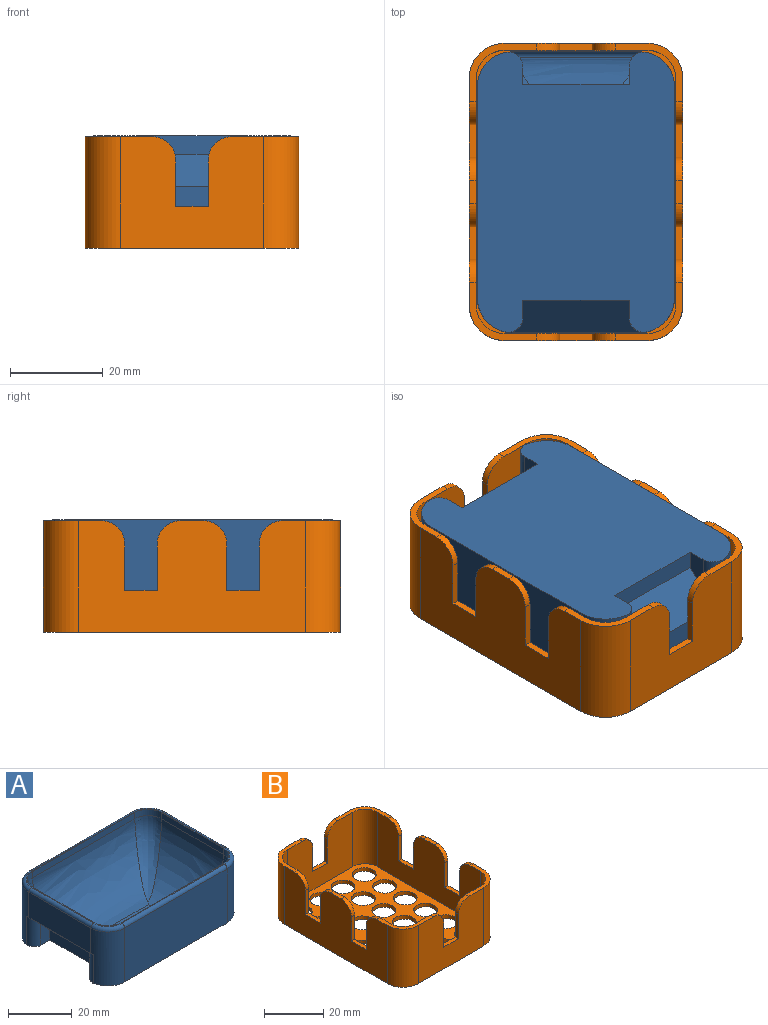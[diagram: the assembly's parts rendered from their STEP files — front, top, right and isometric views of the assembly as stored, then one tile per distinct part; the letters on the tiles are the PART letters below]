
ASSEMBLY  parts=2 mates=1
PART A: 47 faces, bbox 63.4x45.4x23.6 mm
  f0: plane 60.37x42.5mm, normal (0,0,-1), area 2192.5mm2, adj f3,f5,f6,f7,f8,f9,f28,f29
  f1: plane 58x40mm, normal (0,0,1), area 64.5mm2, adj f10,f11,f12,f13,f15,f16,f17,f18
  f2: plane 27.5x9.75mm, normal (-1,0,0), area 268.1mm2, adj f6,f9,f32,f46
  f3: plane 45.5x20.75mm, normal (0,-1,0), area 944.1mm2, adj f0,f6,f7,f42
  f4: plane 27.5x9.75mm, normal (1,0,0), area 268.1mm2, adj f7,f8,f27,f39
  f5: plane 45.5x20.75mm, normal (0,1,0), area 944.1mm2, adj f0,f8,f9,f43
  f6: cylinder r=7.5mm len=20.75mm, axis (0,0,1), area 230.7mm2, adj f0,f2,f3,f32,f38,f44
  f7: cylinder r=7.5mm len=20.75mm, axis (0,0,-1), area 230.7mm2, adj f0,f3,f4,f27,f36,f40
  f8: cylinder r=7.5mm len=20.75mm, axis (0,0,1), area 230.7mm2, adj f0,f4,f5,f27,f35,f41
  f9: cylinder r=7.5mm len=20.75mm, axis (0,0,-1), area 230.7mm2, adj f0,f2,f5,f32,f37,f45
  f10: plane 27.5x2.4mm, normal (1,0,0), area 66mm2, adj f1,f15,f18,f26
  f11: plane 45.5x2.4mm, normal (0,1,0), area 109.2mm2, adj f1,f15,f16,f22
  f12: plane 27.5x2.4mm, normal (-1,0,0), area 66mm2, adj f1,f16,f17,f19
  f13: plane 45.5x2.4mm, normal (0,-1,0), area 109.2mm2, adj f1,f17,f18,f23
  f14: plane 21.3x3.3mm, normal (0,0,1), area 70.3mm2, adj f19,f22,f23,f26
  f15: cylinder r=5.9mm len=5.9mm, axis (0,0,1), area 22.2mm2, adj f1,f10,f11,f24
  f16: cylinder r=5.9mm len=5.9mm, axis (0,0,-1), area 22.2mm2, adj f1,f11,f12,f20
  f17: cylinder r=5.9mm len=5.9mm, axis (0,0,1), area 22.2mm2, adj f1,f12,f13,f21
  f18: cylinder r=5.9mm len=5.9mm, axis (0,0,-1), area 22.2mm2, adj f1,f10,f13,f25
  f19: bspline ~27.5x18mm, area 524mm2, adj f12,f14,f20,f21
  f20: bspline ~19.65x18mm, area 121.3mm2, adj f16,f19,f22
  f21: bspline ~19.65x18mm, area 121.3mm2, adj f17,f19,f23
  f22: bspline ~45.5x18mm, area 941.5mm2, adj f11,f14,f20,f24
  f23: bspline ~45.5x18mm, area 941.5mm2, adj f13,f14,f21,f25
  f24: bspline ~19.65x18mm, area 121.3mm2, adj f15,f22,f26
  f25: bspline ~19.65x18mm, area 121.3mm2, adj f18,f23,f26
  f26: bspline ~27.5x18mm, area 521.8mm2, adj f10,f14,f24,f25
  f27: plane 31.65x8.65mm, normal (0.71,0,-0.71), area 233.7mm2, adj f4,f7,f8,f28,f29,f30,f35,f36
  f28: plane 23x4mm, normal (1,0,0), area 92mm2, adj f0,f27,f29,f30
  f29: plane 7.94x3.94mm, normal (0,1,0), area 23.5mm2, adj f0,f27,f28,f36
  f30: plane 7.94x3.94mm, normal (0,-1,0), area 23.5mm2, adj f0,f27,f28,f35
  f31: plane 23x4mm, normal (-1,0,0), area 92mm2, adj f0,f32,f33,f34
  f32: plane 31.65x8.65mm, normal (-0.71,0,-0.71), area 233.7mm2, adj f2,f6,f9,f31,f33,f34,f37,f38
  f33: plane 7.94x3.94mm, normal (0,1,0), area 23.5mm2, adj f0,f31,f32,f38
  f34: plane 7.94x3.94mm, normal (0,-1,0), area 23.5mm2, adj f0,f31,f32,f37
  f35: cylinder r=3mm len=10.9mm, axis (0,0,1), area 49.1mm2, adj f0,f8,f27,f30
  f36: cylinder r=3mm len=10.9mm, axis (0,0,-1), area 49.1mm2, adj f0,f7,f27,f29
  f37: cylinder r=3mm len=10.9mm, axis (0,0,-1), area 49.1mm2, adj f0,f9,f32,f34
  f38: cylinder r=3mm len=10.9mm, axis (0,0,1), area 49.1mm2, adj f0,f6,f32,f33
  f39: cylinder r=1.25mm len=27.5mm, axis (0,-1,0), area 54mm2, adj f1,f4,f40,f41
  f40: torus R=6.25mm, axis (0,0,1), area 21.7mm2, adj f1,f7,f39,f42
  f41: torus R=6.25mm, axis (0,0,1), area 21.7mm2, adj f1,f8,f39,f43
  f42: cylinder r=1.25mm len=45.5mm, axis (-1,0,0), area 89.3mm2, adj f1,f3,f40,f44
  f43: cylinder r=1.25mm len=45.5mm, axis (1,0,0), area 89.3mm2, adj f1,f5,f41,f45
  f44: torus R=6.25mm, axis (0,0,1), area 21.7mm2, adj f1,f6,f42,f46
  f45: torus R=6.25mm, axis (0,0,1), area 21.7mm2, adj f1,f9,f43,f46
  f46: cylinder r=1.25mm len=27.5mm, axis (0,1,0), area 54mm2, adj f1,f2,f44,f45
PART B: 78 faces, bbox 46x64x24 mm
  f0: plane 14.5x12.5mm, normal (0,0,1), area 33.9mm2, adj f3,f5,f9,f11,f18,f23,f66,f75
  f1: plane 14.5x12.5mm, normal (0,0,1), area 33.9mm2, adj f2,f4,f9,f11,f15,f20,f68,f76
  f2: plane 31x24mm, normal (0,-1,0), area 628.3mm2, adj f1,f13,f14,f15,f16,f63,f64,f65
  f3: plane 31x24mm, normal (0,1,0), area 628.3mm2, adj f0,f8,f14,f17,f18,f60,f61,f62
  f4: plane 31x22.5mm, normal (0,1,0), area 581.8mm2, adj f1,f13,f19,f20,f21,f63,f64,f65
  f5: plane 31x22.5mm, normal (0,-1,0), area 581.8mm2, adj f0,f8,f19,f22,f23,f60,f61,f62
  f6: plane 5x1.5mm, normal (0,0,1), area 7.5mm2, adj f9,f11,f74,f77
  f7: plane 5x1.5mm, normal (0,0,1), area 7.5mm2, adj f10,f12,f70,f72
  f8: plane 14.5x12.5mm, normal (0,0,1), area 33.9mm2, adj f3,f5,f10,f12,f17,f22,f67,f73
  f9: plane 49x24mm, normal (-1,0,0), area 944.5mm2, adj f0,f1,f6,f14,f15,f18,f30,f31
  f10: plane 49x24mm, normal (1,0,0), area 944.5mm2, adj f7,f8,f13,f14,f16,f17,f24,f25
  f11: plane 49x22.5mm, normal (1,0,0), area 871mm2, adj f0,f1,f6,f19,f20,f23,f30,f31
  f12: plane 49x22.5mm, normal (-1,0,0), area 871mm2, adj f7,f8,f13,f19,f21,f22,f24,f25
  f13: plane 14.5x12.5mm, normal (0,0,1), area 33.9mm2, adj f2,f4,f10,f12,f16,f21,f69,f71
  f14: plane 64x46mm, normal (0,0,-1), area 1689.3mm2, adj f2,f3,f9,f10,f15,f16,f17,f18
  f15: cylinder r=7.5mm len=24mm, axis (0,0,1), area 282.7mm2, adj f1,f2,f9,f14
  f16: cylinder r=7.5mm len=24mm, axis (0,0,-1), area 282.7mm2, adj f2,f10,f13,f14
  f17: cylinder r=7.5mm len=24mm, axis (0,0,1), area 282.7mm2, adj f3,f8,f10,f14
  f18: cylinder r=7.5mm len=24mm, axis (0,0,-1), area 282.7mm2, adj f0,f3,f9,f14
  f19: plane 61x43mm, normal (0,0,1), area 1385.7mm2, adj f4,f5,f11,f12,f20,f21,f22,f23
  f20: cylinder r=6mm len=22.5mm, axis (0,0,1), area 212.1mm2, adj f1,f4,f11,f19
  f21: cylinder r=6mm len=22.5mm, axis (0,0,-1), area 212.1mm2, adj f4,f12,f13,f19
  f22: cylinder r=6mm len=22.5mm, axis (0,0,1), area 212.1mm2, adj f5,f8,f12,f19
  f23: cylinder r=6mm len=22.5mm, axis (0,0,-1), area 212.1mm2, adj f0,f5,f11,f19
  f24: plane 10x1.5mm, normal (0,-1,0), area 15mm2, adj f10,f12,f25,f73
  f25: plane 7x1.5mm, normal (0,0,1), area 10.5mm2, adj f10,f12,f24,f26
  f26: plane 10x1.5mm, normal (0,1,0), area 15mm2, adj f10,f12,f25,f72
  f27: plane 7x1.5mm, normal (0,0,1), area 10.5mm2, adj f10,f12,f28,f29
  f28: plane 10x1.5mm, normal (0,1,0), area 15mm2, adj f10,f12,f27,f71
  f29: plane 10x1.5mm, normal (0,-1,0), area 15mm2, adj f10,f12,f27,f70
  f30: plane 10x1.5mm, normal (0,1,0), area 15mm2, adj f9,f11,f31,f74
  f31: plane 7x1.5mm, normal (0,0,1), area 10.5mm2, adj f9,f11,f30,f32
  f32: plane 10x1.5mm, normal (0,-1,0), area 15mm2, adj f9,f11,f31,f75
  f33: plane 10x1.5mm, normal (0,-1,0), area 15mm2, adj f9,f11,f35,f77
  f34: plane 10x1.5mm, normal (0,1,0), area 15mm2, adj f9,f11,f35,f76
  f35: plane 7x1.5mm, normal (0,0,1), area 10.5mm2, adj f9,f11,f33,f34
  f36: cylinder r=4mm len=8mm, axis (0,0,1), area 37.7mm2, adj f14,f19
  f37: cylinder r=4mm len=8mm, axis (0,0,1), area 37.7mm2, adj f14,f19
  f38: cylinder r=4mm len=8mm, axis (0,0,1), area 37.7mm2, adj f14,f19
  f39: cylinder r=4mm len=8mm, axis (0,0,1), area 37.7mm2, adj f14,f19
  f40: cylinder r=4mm len=8mm, axis (0,0,1), area 37.7mm2, adj f14,f19
  f41: cylinder r=4mm len=8mm, axis (0,0,1), area 37.7mm2, adj f14,f19
  f42: cylinder r=4mm len=8mm, axis (0,0,1), area 37.7mm2, adj f14,f19
  f43: cylinder r=4mm len=8mm, axis (0,0,1), area 37.7mm2, adj f14,f19
  f44: cylinder r=4mm len=8mm, axis (0,0,1), area 37.7mm2, adj f14,f19
  f45: cylinder r=4mm len=8mm, axis (0,0,1), area 37.7mm2, adj f14,f19
  f46: cylinder r=4mm len=8mm, axis (0,0,1), area 37.7mm2, adj f14,f19
  f47: cylinder r=4mm len=8mm, axis (0,0,1), area 37.7mm2, adj f14,f19
  f48: cylinder r=4mm len=8mm, axis (0,0,1), area 37.7mm2, adj f14,f19
  f49: cylinder r=4mm len=8mm, axis (0,0,1), area 37.7mm2, adj f14,f19
  f50: cylinder r=4mm len=8mm, axis (0,0,1), area 37.7mm2, adj f14,f19
  f51: cylinder r=4mm len=8mm, axis (0,0,1), area 37.7mm2, adj f14,f19
  f52: cylinder r=4mm len=8mm, axis (0,0,1), area 37.7mm2, adj f14,f19
  f53: cylinder r=4mm len=8mm, axis (0,0,1), area 37.7mm2, adj f14,f19
  f54: cylinder r=4mm len=8mm, axis (0,0,1), area 37.7mm2, adj f14,f19
  f55: cylinder r=4mm len=8mm, axis (0,0,1), area 37.7mm2, adj f14,f19
  f56: cylinder r=4mm len=8mm, axis (0,0,1), area 37.7mm2, adj f14,f19
  f57: cylinder r=4mm len=8mm, axis (0,0,1), area 37.7mm2, adj f14,f19
  f58: cylinder r=4mm len=8mm, axis (0,0,1), area 37.7mm2, adj f14,f19
  f59: cylinder r=4mm len=8mm, axis (0,0,1), area 37.7mm2, adj f14,f19
  f60: plane 7x1.5mm, normal (0,0,1), area 10.5mm2, adj f3,f5,f61,f62
  f61: plane 10x1.5mm, normal (-1,0,0), area 15mm2, adj f3,f5,f60,f67
  f62: plane 10x1.5mm, normal (1,0,0), area 15mm2, adj f3,f5,f60,f66
  f63: plane 10x1.5mm, normal (1,0,0), area 15mm2, adj f2,f4,f65,f68
  f64: plane 10x1.5mm, normal (-1,0,0), area 15mm2, adj f2,f4,f65,f69
  f65: plane 7x1.5mm, normal (0,0,1), area 10.5mm2, adj f2,f4,f63,f64
  f66: cylinder r=5mm len=5mm, axis (0,1,0), area 11.8mm2, adj f0,f3,f5,f62
  f67: cylinder r=5mm len=5mm, axis (0,-1,0), area 11.8mm2, adj f3,f5,f8,f61
  f68: cylinder r=5mm len=5mm, axis (0,1,0), area 11.8mm2, adj f1,f2,f4,f63
  f69: cylinder r=5mm len=5mm, axis (0,-1,0), area 11.8mm2, adj f2,f4,f13,f64
  f70: cylinder r=5mm len=5mm, axis (1,0,0), area 11.8mm2, adj f7,f10,f12,f29
  f71: cylinder r=5mm len=5mm, axis (1,0,0), area 11.8mm2, adj f10,f12,f13,f28
  f72: cylinder r=5mm len=5mm, axis (-1,0,0), area 11.8mm2, adj f7,f10,f12,f26
  f73: cylinder r=5mm len=5mm, axis (-1,0,0), area 11.8mm2, adj f8,f10,f12,f24
  f74: cylinder r=5mm len=5mm, axis (-1,0,0), area 11.8mm2, adj f6,f9,f11,f30
  f75: cylinder r=5mm len=5mm, axis (-1,0,0), area 11.8mm2, adj f0,f9,f11,f32
  f76: cylinder r=5mm len=5mm, axis (1,0,0), area 11.8mm2, adj f1,f9,f11,f34
  f77: cylinder r=5mm len=5mm, axis (1,0,0), area 11.8mm2, adj f6,f9,f11,f33
PLACE A rot(axis=(0.71,0.71,0),180deg) t=(-67.71,-33.66,36.89)mm
PLACE B t=(-69.46,-35.36,12.69)mm
MATE parallel A.f2 <-> B.f4  axis (0,-1,0) through (-46.46,-33.66,21.02)mm
